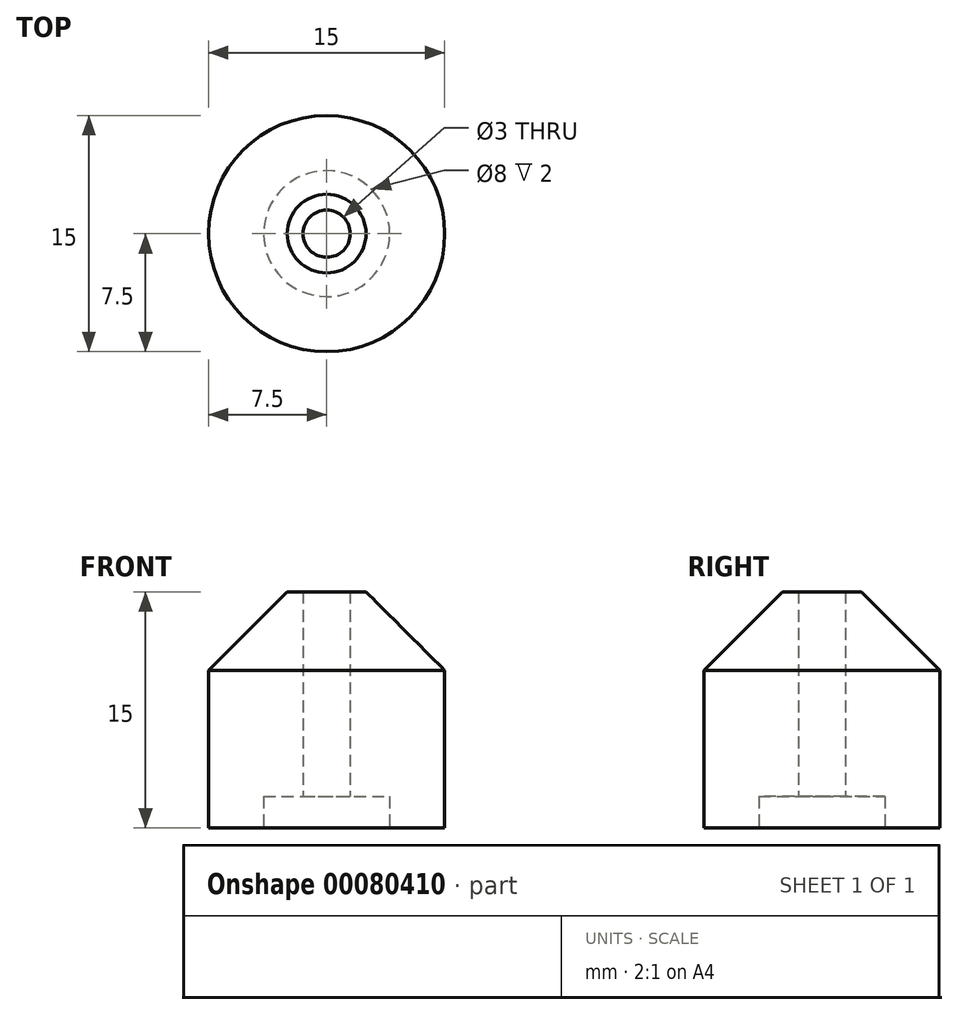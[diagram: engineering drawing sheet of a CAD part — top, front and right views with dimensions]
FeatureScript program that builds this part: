
annotation { "Feature Type Name" : "Feature", "Feature Type Description" : "" }
export const myFeature = defineFeature(function(context is Context, id is Id, definition is map)
    precondition{}
    {
        {
            var Q0;
            Q0=qCreatedBy(makeId("Top.planeOp"),FACE);
            var sketch = newSketch(context, id + "F0", { "sketchPlane" : qUnion([Q0])});
            skCircle(sketch, "E0", {"center": v(0, 0) * mm, "radius": 7.5 * mm});
            skCircle(sketch, "E1", {"center": v(0, 0) * mm, "radius": 1.5 * mm});
            skSolve(sketch);
        }
        {
            var Q0;
            Q0 = qSketchRegion(id + "F0", true);
            extrude(context, id + "F1", {"entities" : qUnion([Q0]), "depth" : 15 * mm});
        }
        {
            var Q0;
            Q0=makeQuery(id+"F1.opExtrude","CAP_EDGE",EDGE,{"disambiguationData":[OSD([sQuery(id+"F0.wireOp",EDGE,"E0")])],"isStart":false});
            chamfer(context, id + "F2", {"entities" : qUnion([Q0]), "width" : 5 * mm, "tangentPropagation" : true});
        }
        {
            var Q0;
            Q0=makeQuery(id+"F1.opExtrude","CAP_FACE",FACE,{"disambiguationData":[OSD([sQuery(id+"F0.wireOp",EDGE,"E0"),sQuery(id+"F0.wireOp",EDGE,"E1")])],"isStart":true});
            var sketch = newSketch(context, id + "F3", { "sketchPlane" : qUnion([Q0])});
            skCircle(sketch, "E2", {"center": v(0, 0) * mm, "radius": 4 * mm});
            skSolve(sketch);
        }
        {
            var Q0;
            Q0 = qSketchRegion(id + "F3", true);
            extrude(context, id + "F4", {"entities" : qUnion([Q0]), "operationType" : NewBodyOperationType.REMOVE, "oppositeDirection" : true, "depth" : 2 * mm});
        }
    });
